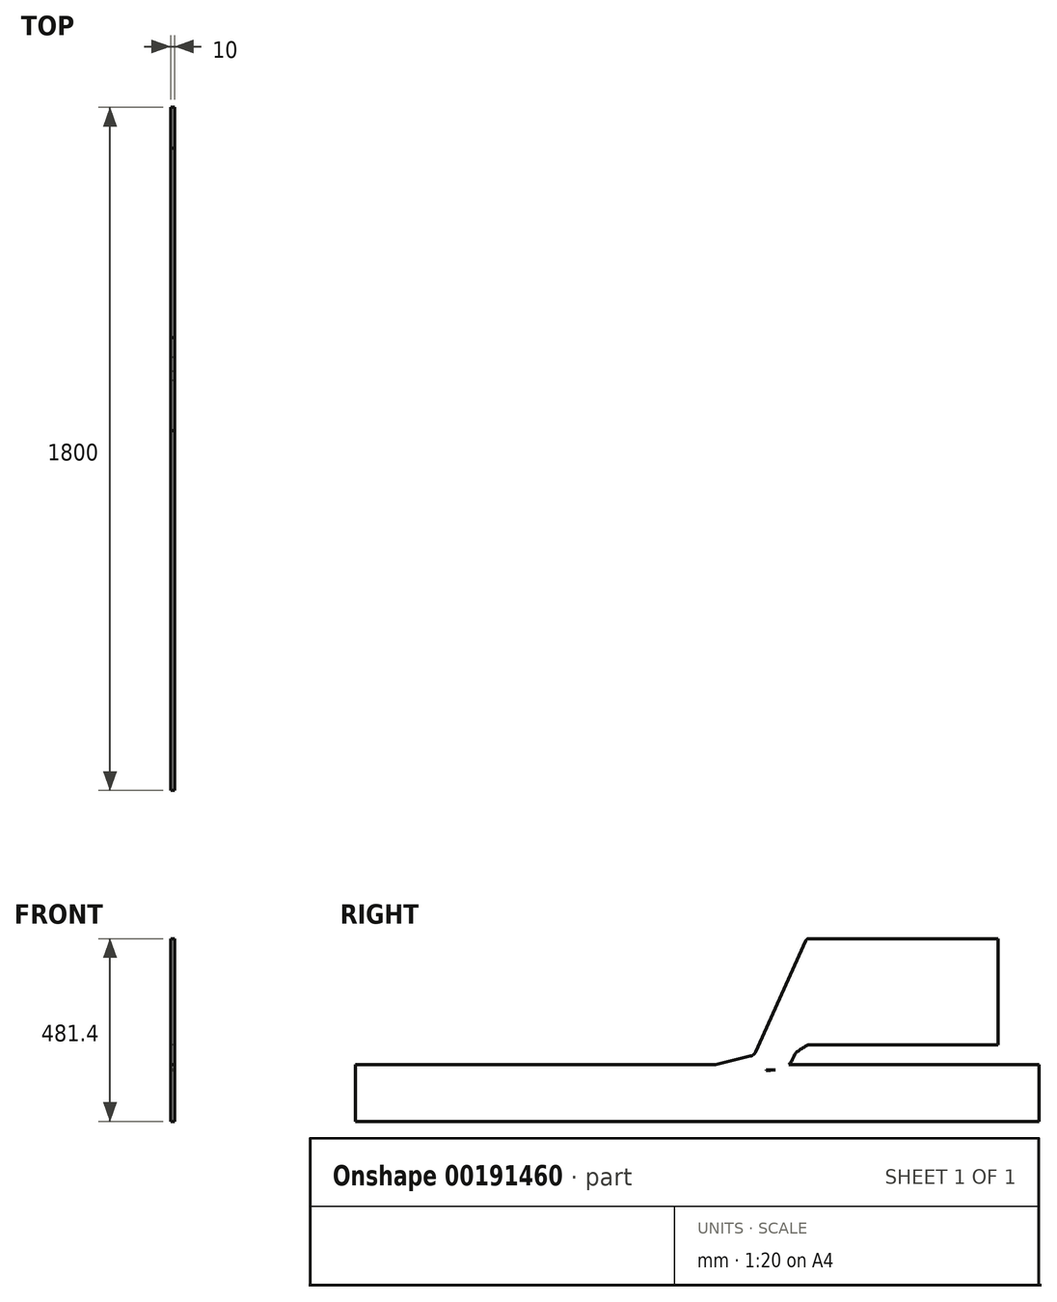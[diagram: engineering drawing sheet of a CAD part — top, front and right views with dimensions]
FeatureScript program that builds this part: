
annotation { "Feature Type Name" : "Feature", "Feature Type Description" : "" }
export const myFeature = defineFeature(function(context is Context, id is Id, definition is map)
    precondition{}
    {
        {
            var Q0;
            Q0=qCreatedBy(makeId("Front.planeOp"),FACE);
            var sketch = newSketch(context, id + "F0", { "sketchPlane" : qUnion([Q0])});
            skLineSegment(sketch, "E0.bottom", {"start": v(-72.14, 0) * mm, "end": v(927.86, 0) * mm});
            skLineSegment(sketch, "E0.top", {"start": v(-72.14, -150) * mm, "end": v(927.86, -150) * mm});
            skLineSegment(sketch, "E0.left", {"start": v(-72.14, 0) * mm, "end": v(-72.14, -150) * mm});
            skLineSegment(sketch, "E0.right", {"start": v(927.86, 0) * mm, "end": v(927.86, -150) * mm});
            skSolve(sketch);
        }
        {
            var Q0;
            Q0 = qSketchRegion(id + "F0", true);
            extrude(context, id + "F1", {"entities" : qUnion([Q0]), "depth" : 1800 * mm});
        }
        {
            var Q0;
            Q0=makeQuery(id+"F1.opExtrude","CAP_EDGE",EDGE,{"disambiguationData":[OSD([sQuery(id+"F0.wireOp",EDGE,"E0.bottom")])],"isStart":true});
            cPoint(context, id + "F2", {"entities" : qUnion([Q0]), "parameter" : 0.5});
        }
        {
            var Q0;
            Q0=qCreatedBy(makeId("Right.planeOp"),FACE);
            var Q1;
            Q1 = qCreatedBy(id + "F2" ,VERTEX);
            cPlane(context, id + "F3", {"entities" : qUnion([Q0, Q1]), "cplaneType" : CPlaneType.PLANE_POINT, "offset" : 25 * mm, "width" : 150 * mm, "height" : 150 * mm});
        }
        {
            var Q0;
            Q0=qCreatedBy(id+"F3.planeOp",FACE);
            var sketch = newSketch(context, id + "F4", { "sketchPlane" : qUnion([Q0])});
            skFitSpline(sketch, "E1", {"points": [v(-658.51, 0) * mm, v(-674.82, -9.28) * mm, v(-718.06, -15.01) * mm], "startDerivative": vector(-34.83, -25.75) * mm, "endDerivative": vector(-80.73, -5.2) * mm});
            skFitSpline(sketch, "E2", {"points": [v(-658.51, 0) * mm, v(-642.03, 27.37) * mm, v(-607.35, 51.78) * mm], "startDerivative": vector(52.63, 38.91) * mm, "endDerivative": vector(55, 31.26) * mm});
            skLineSegment(sketch, "E3", {"start": v(-851.83, 0) * mm, "end": v(-759.92, 21.64) * mm});
            skLineSegment(sketch, "E4", {"start": v(-607.35, 51.78) * mm, "end": v(-607.35, 331.4) * mm});
            skLineSegment(sketch, "E5", {"start": v(-746.28, 32.86) * mm, "end": v(-613.73, 325.9) * mm});
            skPoint(sketch, "E6.visualSharp", {"position": v(-750.33, 23.9) * mm});
            skArc(sketch, "E6.filletArc", {"start": v(-759.92, 21.64) * mm, "mid": v(-751.8, 25.66) * mm, "end": v(-746.28, 32.86) * mm});
            skArc(sketch, "E7.filletArc", {"start": v(-607.35, 331.4) * mm, "mid": v(-611.15, 329.35) * mm, "end": v(-613.73, 325.9) * mm});
            skLineSegment(sketch, "E8", {"start": v(-851.83, 0) * mm, "end": v(-724.44, 0) * mm});
            skLineSegment(sketch, "E9", {"start": v(-718.06, -15.01) * mm, "end": v(-724.44, 0) * mm});
            skSolve(sketch);
        }
        {
            var Q0;
            Q0 = qSketchRegion(id + "F4", true);
            extrude(context, id + "F5", {"entities" : qUnion([Q0]), "operationType" : NewBodyOperationType.ADD, "endBound" : BoundingType.SYMMETRIC, "depth" : 500 * mm});
        }
        {
            var Q0;
            Q0=qCreatedBy(id+"F3.planeOp",FACE);
            var sketch = newSketch(context, id + "F6", { "sketchPlane" : qUnion([Q0])});
            skFitSpline(sketch, "E10.0", {"points": [v(-657.92, -0.8) * mm, v(-659.37, -1.88) * mm, v(-662.3, -4.06) * mm, v(-666.42, -6.67) * mm, v(-670.2, -8.57) * mm, v(-673.31, -9.86) * mm, v(-676.77, -10.98) * mm, v(-681.81, -12.26) * mm, v(-688.82, -13.5) * mm, v(-698.08, -14.57) * mm, v(-707.9, -15.36) * mm, v(-714.63, -15.8) * mm, v(-718, -16) * mm]});
            skLineSegment(sketch, "E11", {"start": v(-657.92, -0.8) * mm, "end": v(-656.83, 0) * mm});
            skFitSpline(sketch, "E12.0", {"points": [v(-658.51, 0) * mm, v(-663.1, -3.4) * mm, v(-674.9, -12.23) * mm, v(-701.8, -13.97) * mm, v(-718.06, -15.01) * mm]});
            skLineSegment(sketch, "E13", {"start": v(-718.06, -15.01) * mm, "end": v(-718, -16) * mm});
            skLineSegment(sketch, "E14", {"start": v(-658.51, 0) * mm, "end": v(-656.83, 0) * mm});
            skSolve(sketch);
        }
        {
            var Q0;
            Q0=makeQuery(id+"F6.imprint","IMPRINT",FACE,{"disambiguationData":[TD([[makeQuery(id+"F6.imprint","IMPRINT",EDGE,{"derivedFrom":sQuery(id+"F6.wireOp",EDGE,"E10.0")}),-1.0]])]});
            extrude(context, id + "F7", {"entities" : qUnion([Q0]), "operationType" : NewBodyOperationType.REMOVE, "endBound" : BoundingType.SYMMETRIC, "oppositeDirection" : true, "depth" : 500 * mm});
        }
        {
            var Q0;
            Q0=qCreatedBy(id+"F3.planeOp",FACE);
            var sketch = newSketch(context, id + "F8", { "sketchPlane" : qUnion([Q0])});
            skLineSegment(sketch, "E15.bottom", {"start": v(0, -155.59) * mm, "end": v(-1814.46, -155.59) * mm});
            skLineSegment(sketch, "E15.top", {"start": v(0, 520.8) * mm, "end": v(-1814.46, 520.8) * mm});
            skLineSegment(sketch, "E15.left", {"start": v(0, -155.59) * mm, "end": v(0, 520.8) * mm});
            skLineSegment(sketch, "E15.right", {"start": v(-1814.46, -155.59) * mm, "end": v(-1814.46, 520.8) * mm});
            skSolve(sketch);
        }
        {
            var Q0;
            Q0=makeQuery(id+"F8.imprint","IMPRINT",FACE,{"disambiguationData":[TD([[makeQuery(id+"F8.imprint","IMPRINT",EDGE,{"derivedFrom":sQuery(id+"F8.wireOp",EDGE,"E15.bottom")}),-1.0]])]});
            var Q1;
            Q1=makeQuery(id+"F1.opExtrude","SWEPT_FACE",FACE,{"disambiguationData":[OSD([sQuery(id+"F0.wireOp",EDGE,"E0.right")])]});
            extrude(context, id + "F9", {"entities" : qUnion([Q0]), "operationType" : NewBodyOperationType.REMOVE, "endBound" : BoundingType.UP_TO_SURFACE, "endBoundEntityFace" : qUnion([Q1]), "depth" : 500 * mm});
        }
        {
            var Q0;
            Q0=makeQuery(id+"F5.opExtrude","SWEPT_FACE",FACE,{"disambiguationData":[OSD([sQuery(id+"F4.wireOp",EDGE,"E4")])]});
            extrude(context, id + "F10", {"entities" : qUnion([Q0]), "operationType" : NewBodyOperationType.ADD, "depth" : 500 * mm});
        }
        {
            var Q0;
            Q0=makeQuery(id+"F1.opExtrude","SWEPT_FACE",FACE,{"disambiguationData":[OSD([sQuery(id+"F0.wireOp",EDGE,"E0.left")])]});
            var sketch = newSketch(context, id + "F11", { "sketchPlane" : qUnion([Q0])});
            skLineSegment(sketch, "E16.bottom", {"start": v(-27.55, -220.66) * mm, "end": v(1848.53, -220.66) * mm});
            skLineSegment(sketch, "E16.top", {"start": v(-27.55, 364.3) * mm, "end": v(1848.53, 364.3) * mm});
            skLineSegment(sketch, "E16.left", {"start": v(-27.55, -220.66) * mm, "end": v(-27.55, 364.3) * mm});
            skLineSegment(sketch, "E16.right", {"start": v(1848.53, -220.66) * mm, "end": v(1848.53, 364.3) * mm});
            skSolve(sketch);
        }
        {
            var Q0;
            Q0 = qSketchRegion(id + "F11", true);
            var Q1;
            {var subQ0=sQuery(id+"F8.wireOp",EDGE,"E15.right");var subQ1=sQuery(id+"F8.wireOp",EDGE,"E15.left");var subQ2=sQuery(id+"F8.wireOp",EDGE,"E15.top");var subQ3=sQuery(id+"F8.wireOp",EDGE,"E15.bottom");Q1=makeQuery(id+"F10.boolean.opBoolean","MERGE",FACE,{"derivedFrom":[makeQuery(id+"F9.boolean.opBoolean","COPY",FACE,{"derivedFrom":makeQuery(id+"F9.opExtrude","CAP_FACE",FACE,{"disambiguationData":[OSD([subQ3,subQ2,subQ1,subQ0])],"isStart":true})}),makeQuery(id+"F10.opExtrude","SWEPT_FACE",FACE,{"disambiguationData":[OSD([sQuery(id+"F4.wireOp",EDGE,"E4"),subQ3,subQ2,subQ1,subQ0])]})]});}
            extrude(context, id + "F12", {"entities" : qUnion([Q0]), "operationType" : NewBodyOperationType.REMOVE, "oppositeDirection" : true, "endBoundEntityFace" : qUnion([Q1]), "depth" : 490 * mm});
        }
    });
